# Revit family: БА50_220_RV17_LOD400 (05.11.23)
name_source: partatom
category: Электрооборудование
revit_build: Autodesk Revit 2017 (Build: 20170118_1100(x64)
units: mm (PartAtom-declared; Revit-internal decimal feet)

## family parameters
Всегда вертикально = Нет
Конфигурация панели = Два столбца, слева направо
На основе рабочей плоскости = Да
Общий = Нет
При загрузке вырезать с полостями = Нет
Размер круглого соединителя = Использовать диаметр
Тип детали = Щит
Точка расчета площади = Нет

## types (1)
- БА50/220
    ADSK_URL страницы изделия = https://stilsoft.ru
    ADSK_Единица измерения = шт.
    ADSK_Завод-изготовитель = ООО «Основа Безопасности»
    ADSK_Количество = 1
    ADSK_Марка = СТВФ.426471.125
    ADSK_Масса = 2.5
    ADSK_Наименование = Аудиоусилитель БА50/220
    ADSK_Размер_Высота = 64 мм
    ADSK_Размер_Глубина = 202 мм
    ADSK_Размер_Длина = 286 мм
    d_короба = 20 мм
    Время непрерывной работы, ч = круглосуточно
    Диапазон воспроизводимых частот, Гц = 20... 15000
    Диапазон рабочих температур, °С = от – 40 до + 50
    Долговременная выходная мощность, Вт = 2 х 22
    Интерфейс связи = 10BaseT/100Base TX Ethernet
    Количество аудиоканалов, шт = 2
    Коэффициент усиления по напряжению Au, дБ = 45
    Мощность = 44
    Напряжение = 220
    Номинальный потребляемый ток, не более, А = 0 А
    Отметка по умолчанию = 1219 мм
